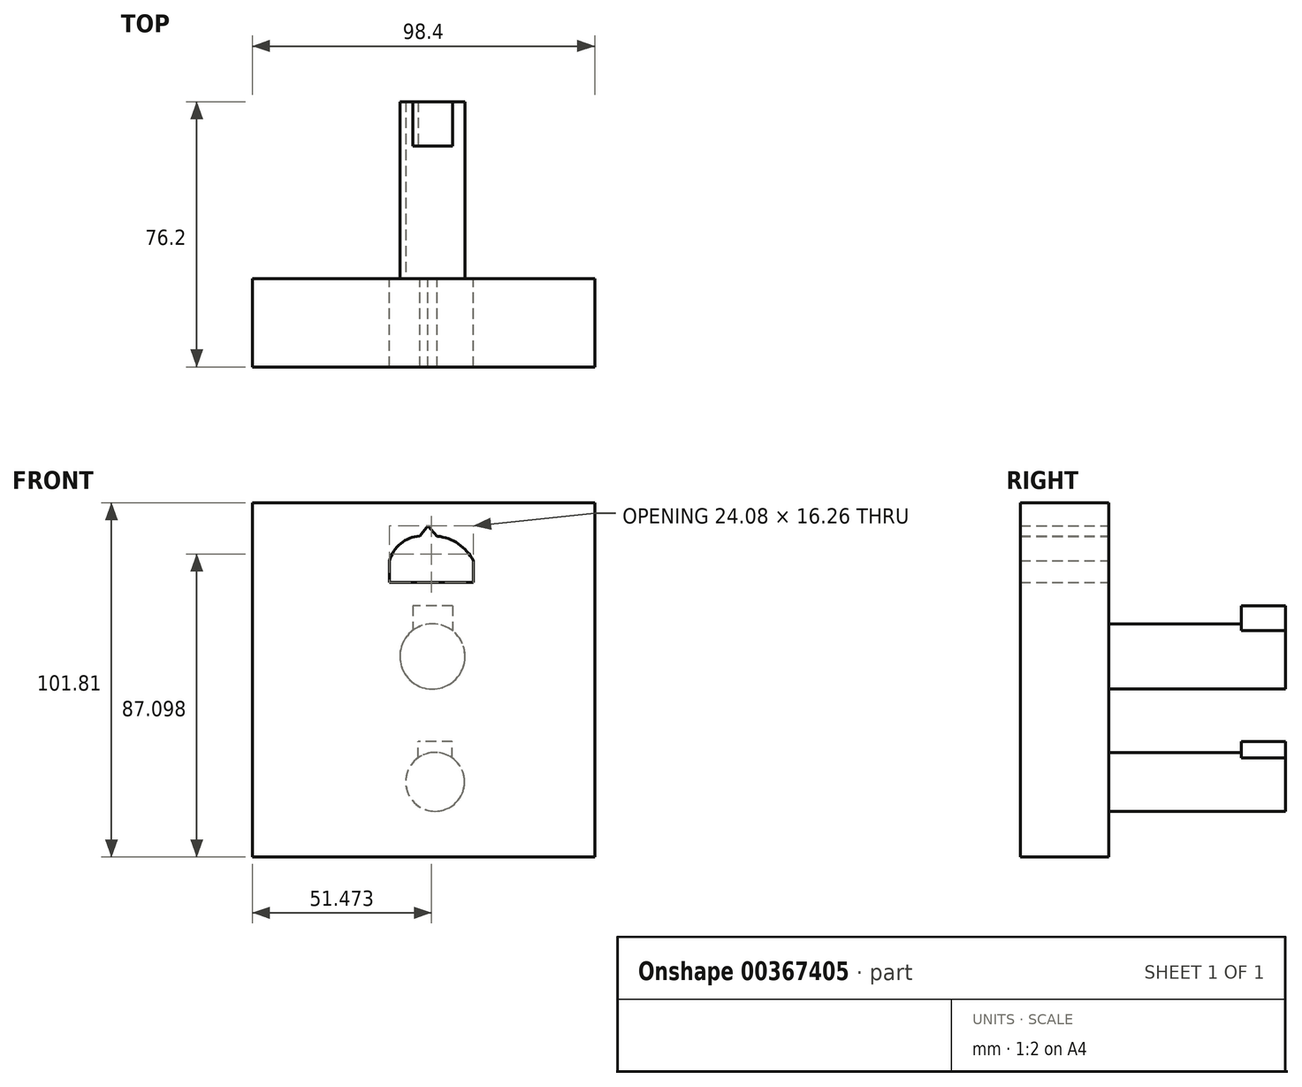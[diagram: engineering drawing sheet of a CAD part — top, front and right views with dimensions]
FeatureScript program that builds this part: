
annotation { "Feature Type Name" : "Feature", "Feature Type Description" : "" }
export const myFeature = defineFeature(function(context is Context, id is Id, definition is map)
    precondition{}
    {
        {
            var Q0;
            Q0=qCreatedBy(makeId("Front.planeOp"),FACE);
            var sketch = newSketch(context, id + "F0", { "sketchPlane" : qUnion([Q0])});
            skLineSegment(sketch, "E0.bottom", {"start": v(-50.43, 49.86) * mm, "end": v(67.88, 49.86) * mm});
            skLineSegment(sketch, "E0.top", {"start": v(-50.43, -51.95) * mm, "end": v(67.88, -51.95) * mm});
            skLineSegment(sketch, "E0.left", {"start": v(-50.43, 49.86) * mm, "end": v(-50.43, -51.95) * mm});
            skLineSegment(sketch, "E0.right", {"start": v(67.88, 49.86) * mm, "end": v(67.88, -51.95) * mm});
            skSolve(sketch);
        }
        {
            var Q0;
            Q0 = qSketchRegion(id + "F0", true);
            extrude(context, id + "F1", {"entities" : qUnion([Q0]), "depth" : 25.4 * mm});
        }
        {
            var Q0;
            Q0=qCreatedBy(makeId("Front.planeOp"),FACE);
            var sketch = newSketch(context, id + "F2", { "sketchPlane" : qUnion([Q0])});
            skArc(sketch, "E1", {"start": v(0, 40.17) * mm, "mid": v(-6.86, 38.8) * mm, "end": v(-11, 33.16) * mm});
            skLineSegment(sketch, "E2", {"start": v(-11, 33.16) * mm, "end": v(-11, 27.02) * mm});
            skLineSegment(sketch, "E3", {"start": v(-11, 27.02) * mm, "end": v(13.08, 27.02) * mm});
            skLineSegment(sketch, "E4", {"start": v(13.08, 27.02) * mm, "end": v(13.08, 33.16) * mm});
            skArc(sketch, "E5", {"start": v(13.08, 33.16) * mm, "mid": v(7.66, 38.74) * mm, "end": v(0, 40.17) * mm});
            skSolve(sketch);
        }
        {
            var Q0;
            Q0 = qSketchRegion(id + "F2", true);
            extrude(context, id + "F3", {"entities" : qUnion([Q0]), "operationType" : NewBodyOperationType.REMOVE, "depth" : 25.4 * mm});
        }
        {
            var Q0;
            Q0=qCreatedBy(makeId("Front.planeOp"),FACE);
            var sketch = newSketch(context, id + "F4", { "sketchPlane" : qUnion([Q0])});
            skCircle(sketch, "E6", {"center": v(1.33, 5.69) * mm, "radius": 9.37 * mm});
            skSolve(sketch);
        }
        {
            var Q0;
            Q0 = qSketchRegion(id + "F4", true);
            extrude(context, id + "F5", {"entities" : qUnion([Q0]), "operationType" : NewBodyOperationType.ADD, "oppositeDirection" : true, "depth" : 50.8 * mm});
        }
        {
            var Q0;
            Q0=qCreatedBy(makeId("Front.planeOp"),FACE);
            var sketch = newSketch(context, id + "F6", { "sketchPlane" : qUnion([Q0])});
            skLineSegment(sketch, "E7", {"start": v(47.97, 48.54) * mm, "end": v(47.97, -52.14) * mm});
            skLineSegment(sketch, "E8", {"start": v(47.97, 48.54) * mm, "end": v(47.97, 50.05) * mm});
            skLineSegment(sketch, "E9", {"start": v(47.97, 50.05) * mm, "end": v(47.97, -56.12) * mm});
            skLineSegment(sketch, "E10", {"start": v(47.97, -56.12) * mm, "end": v(47.97, 52.33) * mm});
            skLineSegment(sketch, "E11", {"start": v(47.97, 52.33) * mm, "end": v(47.97, 50.05) * mm});
            skLineSegment(sketch, "E12", {"start": v(71.67, 50.05) * mm, "end": v(47.97, 50.05) * mm});
            skLineSegment(sketch, "E13", {"start": v(67.69, 50.05) * mm, "end": v(67.69, -54.6) * mm});
            skLineSegment(sketch, "E14", {"start": v(67.69, -54.6) * mm, "end": v(67.69, -52.14) * mm});
            skLineSegment(sketch, "E15", {"start": v(67.69, -52.14) * mm, "end": v(47.97, -52.14) * mm});
            skSolve(sketch);
        }
        {
            var Q0;
            Q0 = qSketchRegion(id + "F6", true);
            extrude(context, id + "F7", {"entities" : qUnion([Q0]), "operationType" : NewBodyOperationType.REMOVE, "depth" : 25.4 * mm});
        }
        {
            var Q0;
            Q0=qCreatedBy(makeId("Front.planeOp"),FACE);
            var sketch = newSketch(context, id + "F8", { "sketchPlane" : qUnion([Q0])});
            skLineSegment(sketch, "E16.bottom", {"start": v(64.27, 49.86) * mm, "end": v(70.72, 49.86) * mm});
            skLineSegment(sketch, "E16.top", {"start": v(64.27, -54.98) * mm, "end": v(70.72, -54.98) * mm});
            skLineSegment(sketch, "E16.left", {"start": v(64.27, 49.86) * mm, "end": v(64.27, -54.98) * mm});
            skLineSegment(sketch, "E16.right", {"start": v(70.72, 49.86) * mm, "end": v(70.72, -54.98) * mm});
            skSolve(sketch);
        }
        {
            var Q0;
            Q0 = qSketchRegion(id + "F8", true);
            extrude(context, id + "F9", {"entities" : qUnion([Q0]), "operationType" : NewBodyOperationType.REMOVE, "depth" : 25.4 * mm});
        }
        {
            var Q0;
            Q0=makeQuery(id+"F5.opExtrude","CAP_FACE",FACE,{"disambiguationData":[OSD([sQuery(id+"F4.wireOp",EDGE,"E6")])],"isStart":false});
            var sketch = newSketch(context, id + "F10", { "sketchPlane" : qUnion([Q0])});
            skLineSegment(sketch, "E17.bottom", {"start": v(-7.1, 20.29) * mm, "end": v(4.28, 20.29) * mm});
            skLineSegment(sketch, "E17.top", {"start": v(-7.1, 2.46) * mm, "end": v(4.28, 2.46) * mm});
            skLineSegment(sketch, "E17.left", {"start": v(-7.1, 20.29) * mm, "end": v(-7.1, 2.46) * mm});
            skLineSegment(sketch, "E17.right", {"start": v(4.28, 20.29) * mm, "end": v(4.28, 2.46) * mm});
            skSolve(sketch);
        }
        {
            var Q0;
            Q0 = qSketchRegion(id + "F10", true);
            extrude(context, id + "F11", {"entities" : qUnion([Q0]), "operationType" : NewBodyOperationType.ADD, "oppositeDirection" : true, "depth" : 12.7 * mm});
        }
        {
            var Q0;
            {var subQ0=sQuery(id+"F0.wireOp",EDGE,"E0.left");var subQ1=sQuery(id+"F0.wireOp",EDGE,"E0.top");var subQ2=sQuery(id+"F0.wireOp",EDGE,"E0.bottom");Q0=makeQuery(id+"F7.boolean.opBoolean","SPLIT",FACE,{"disambiguationData":[TD([makeQuery(id+"F1.opExtrude","SWEPT_FACE",FACE,{"disambiguationData":[OSD([subQ0])]})])],"derivedFrom":makeQuery(id+"F1.opExtrude","CAP_FACE",FACE,{"disambiguationData":[OSD([subQ2,subQ1,subQ0,sQuery(id+"F0.wireOp",EDGE,"E0.right")])],"isStart":true})});}
            var sketch = newSketch(context, id + "F12", { "sketchPlane" : qUnion([Q0])});
            skLineSegment(sketch, "E18", {"start": v(4.08, 38.02) * mm, "end": v(0, 43.28) * mm});
            skLineSegment(sketch, "E19", {"start": v(0, 43.28) * mm, "end": v(-4.65, 38.02) * mm});
            skLineSegment(sketch, "E20", {"start": v(4.08, 38.02) * mm, "end": v(-4.65, 38.02) * mm});
            skSolve(sketch);
        }
        {
            var Q0;
            Q0 = qSketchRegion(id + "F12", true);
            extrude(context, id + "F13", {"entities" : qUnion([Q0]), "operationType" : NewBodyOperationType.REMOVE, "oppositeDirection" : true, "depth" : 25.4 * mm});
        }
        {
            var Q0;
            {var subQ0=sQuery(id+"F0.wireOp",EDGE,"E0.left");var subQ1=sQuery(id+"F0.wireOp",EDGE,"E0.top");var subQ2=sQuery(id+"F0.wireOp",EDGE,"E0.bottom");Q0=makeQuery(id+"F7.boolean.opBoolean","SPLIT",FACE,{"disambiguationData":[TD([makeQuery(id+"F1.opExtrude","SWEPT_FACE",FACE,{"disambiguationData":[OSD([subQ0])]})])],"derivedFrom":makeQuery(id+"F1.opExtrude","CAP_FACE",FACE,{"disambiguationData":[OSD([subQ2,subQ1,subQ0,sQuery(id+"F0.wireOp",EDGE,"E0.right")])],"isStart":true})});}
            var sketch = newSketch(context, id + "F14", { "sketchPlane" : qUnion([Q0])});
            skCircle(sketch, "E21", {"center": v(-2.09, -30.34) * mm, "radius": 8.45 * mm});
            skSolve(sketch);
        }
        {
            var Q0;
            Q0 = qSketchRegion(id + "F14", true);
            extrude(context, id + "F15", {"entities" : qUnion([Q0]), "operationType" : NewBodyOperationType.ADD, "depth" : 50.8 * mm});
        }
        {
            var Q0;
            Q0=makeQuery(id+"F15.opExtrude","CAP_FACE",FACE,{"disambiguationData":[OSD([sQuery(id+"F14.wireOp",EDGE,"E21")])],"isStart":false});
            var sketch = newSketch(context, id + "F16", { "sketchPlane" : qUnion([Q0])});
            skLineSegment(sketch, "E22.bottom", {"start": v(-7.02, -35.27) * mm, "end": v(2.84, -35.27) * mm});
            skLineSegment(sketch, "E22.top", {"start": v(-7.02, -18.77) * mm, "end": v(2.84, -18.77) * mm});
            skLineSegment(sketch, "E22.left", {"start": v(-7.02, -35.27) * mm, "end": v(-7.02, -18.77) * mm});
            skLineSegment(sketch, "E22.right", {"start": v(2.84, -35.27) * mm, "end": v(2.84, -18.77) * mm});
            skSolve(sketch);
        }
        {
            var Q0;
            Q0 = qSketchRegion(id + "F16", true);
            extrude(context, id + "F17", {"entities" : qUnion([Q0]), "operationType" : NewBodyOperationType.ADD, "oppositeDirection" : true, "depth" : 12.7 * mm});
        }
    });
